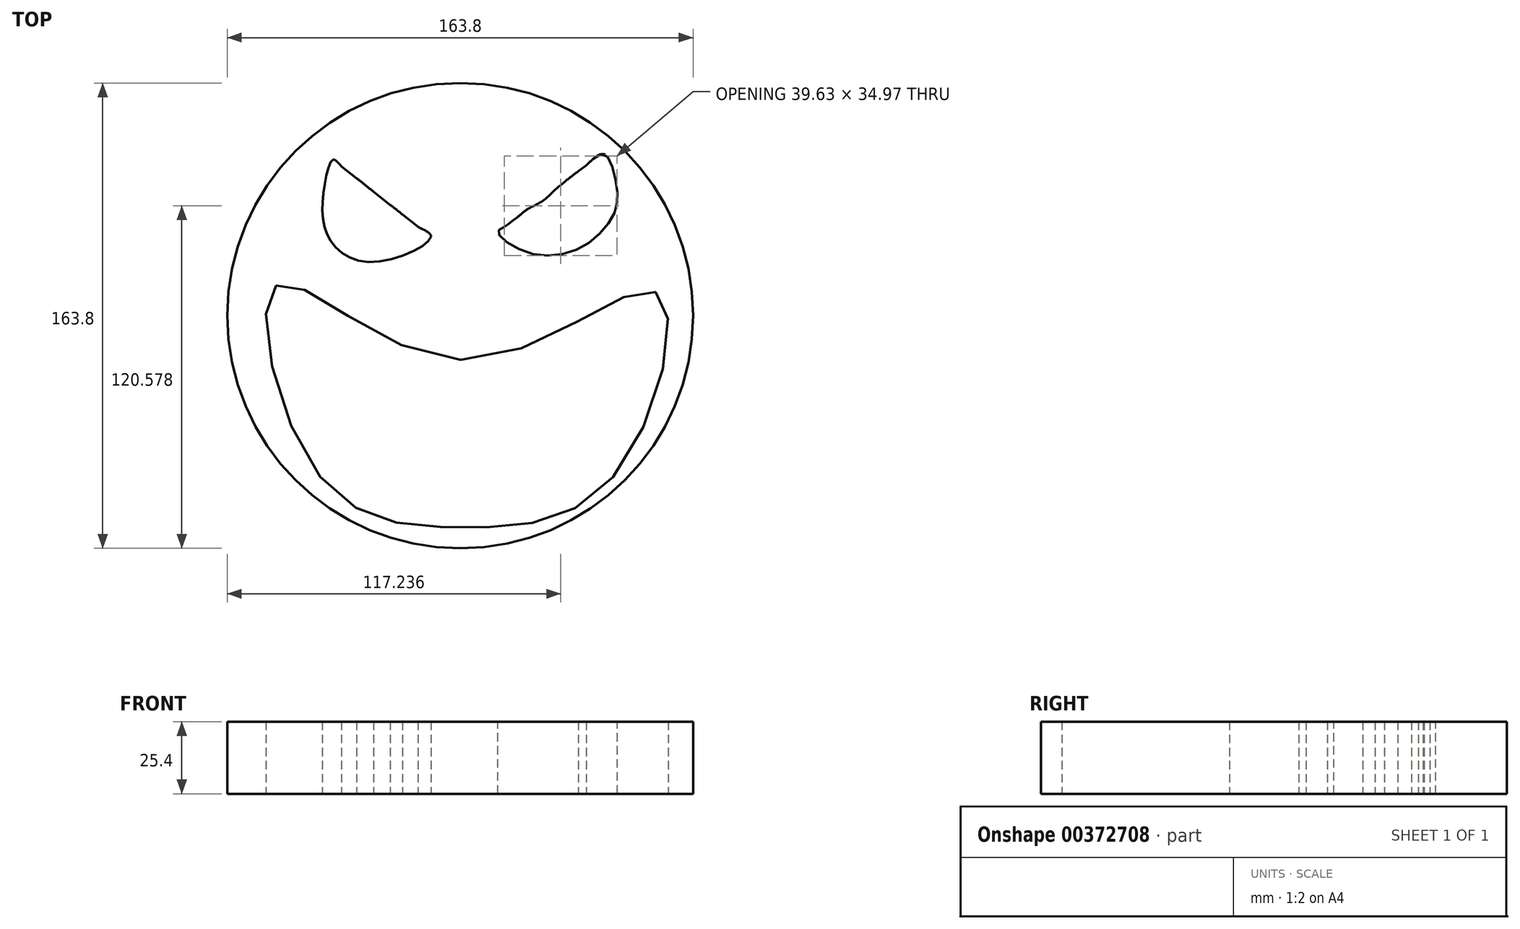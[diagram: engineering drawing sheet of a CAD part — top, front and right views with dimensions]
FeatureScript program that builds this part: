
annotation { "Feature Type Name" : "Feature", "Feature Type Description" : "" }
export const myFeature = defineFeature(function(context is Context, id is Id, definition is map)
    precondition{}
    {
        {
            var Q0;
            Q0=qCreatedBy(makeId("Top.planeOp"),FACE);
            var sketch = newSketch(context, id + "F0", { "sketchPlane" : qUnion([Q0])});
            skCircle(sketch, "E0", {"center": v(0, 0) * mm, "radius": 81.9 * mm});
            skPoint(sketch, "E1.center.orphan", {"position": v(-60.96, 0) * mm});
            skPoint(sketch, "E2.center.orphan", {"position": v(56.08, 0) * mm});
            skPoint(sketch, "E3.center.orphan", {"position": v(0, -33.07) * mm});
            skFitSpline(sketch, "E4", {"points": [v(-64.7, 10.65) * mm, v(0, -15.56) * mm, v(69.29, 8.03) * mm, v(54.22, -56.19) * mm, v(0, -74.53) * mm, v(-49.96, -55.86) * mm, v(-64.7, 10.65) * mm]});
            skLineSegment(sketch, "E5", {"start": v(-44.72, 54.87) * mm, "end": v(-10.32, 27.68) * mm});
            skFitSpline(sketch, "E6", {"points": [v(-10.32, 27.68) * mm, v(-30.96, 18.84) * mm, v(-46.36, 27.68) * mm, v(-48, 43.74) * mm, v(-44.72, 54.87) * mm, v(-41.75, 52.53) * mm, v(-36.5, 48.37) * mm, v(-30.47, 43.61) * mm, v(-24.57, 38.95) * mm, v(-20.35, 35.61) * mm, v(-14.85, 31.27) * mm, v(-10.32, 27.68) * mm]});
            skPoint(sketch, "E7.2.internal.orphan", {"position": v(13.27, 31.16) * mm});
            skPoint(sketch, "E8.0.internal.orphan", {"position": v(13.27, 27.68) * mm});
            skPoint(sketch, "E8.6.internal.orphan", {"position": v(34.22, 44.66) * mm});
            skPoint(sketch, "E9.2.internal.orphan", {"position": v(48.65, 27.68) * mm});
            skPoint(sketch, "E9.4.internal.orphan", {"position": v(44.4, 52.9) * mm});
            skPoint(sketch, "E9.7.internal.orphan", {"position": v(33.82, 44.66) * mm});
            skPoint(sketch, "E9.8.internal.orphan", {"position": v(28.83, 40.3) * mm});
            skLineSegment(sketch, "E10", {"start": v(20.04, 34.66) * mm, "end": v(23.96, 37.6) * mm});
            skFitSpline(sketch, "E11", {"points": [v(13.27, 29.58) * mm, v(22.48, 22.62) * mm, v(41.68, 23.56) * mm, v(53.9, 35.42) * mm, v(54.85, 46.7) * mm, v(50.33, 56.87) * mm, v(44.4, 52.9) * mm, v(41.6, 50.82) * mm, v(33.82, 44.66) * mm, v(28.83, 40.3) * mm, v(23.96, 37.6) * mm, v(20.04, 34.66) * mm, v(17.45, 32.72) * mm, v(15.38, 31.16) * mm, v(13.27, 29.58) * mm]});
            skLineSegment(sketch, "E12.trimOffspring", {"start": v(37.53, 47.77) * mm, "end": v(44.4, 52.9) * mm});
            skSolve(sketch);
        }
        {
            var Q0;
            Q0 = qSketchRegion(id + "F0", true);
            extrude(context, id + "F1", {"entities" : qUnion([Q0]), "depth" : 25.4 * mm});
        }
    });
